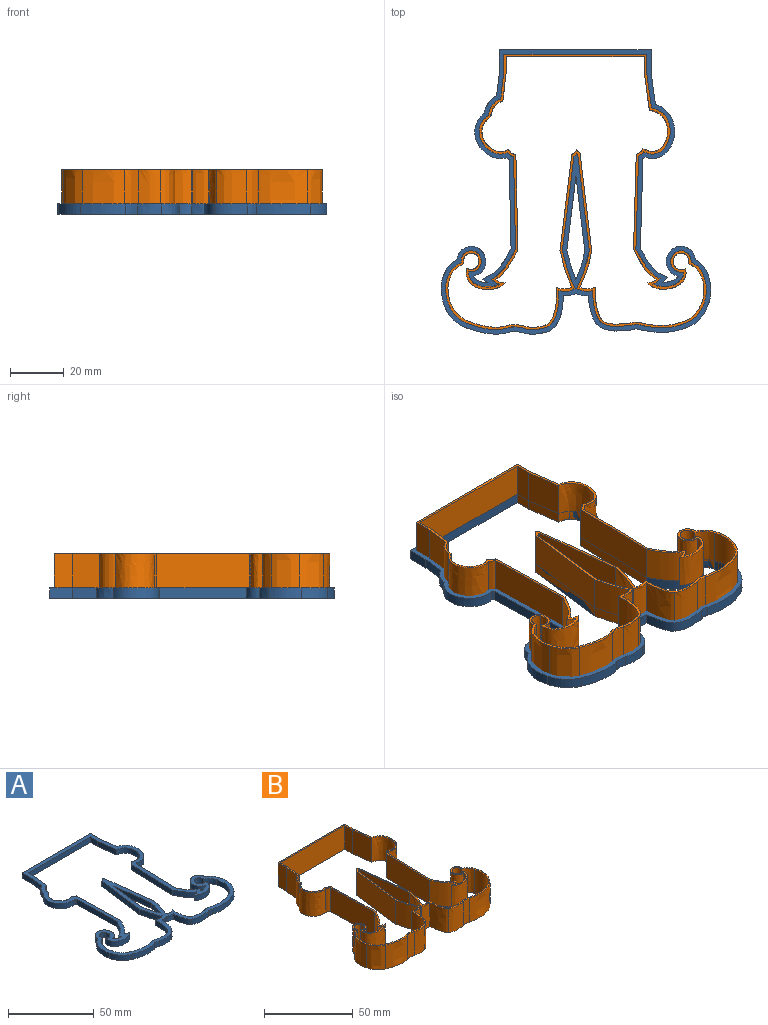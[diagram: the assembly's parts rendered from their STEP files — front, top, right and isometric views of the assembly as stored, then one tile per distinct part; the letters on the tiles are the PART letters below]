
ASSEMBLY  parts=2 mates=1
PART A: 86 faces, bbox 103.2x108.7x6.8 mm
  f0: plane 108.68x103.23mm, normal (0,0,1), area 1482.3mm2, adj f2,f3,f4,f5,f6,f7,f8,f9
  f1: plane 108.68x103.23mm, normal (0,0,-1), area 1482.3mm2, adj f2,f3,f4,f5,f6,f7,f8,f9
  f2: plane 56.38x3.81mm, normal (0,1,0), area 214.8mm2, adj f0,f1,f3,f42
  f3: extruded ~8.41x3.81mm, area 32mm2, adj f0,f1,f2,f4
  f4: plane 8.77x3.81mm, normal (-0.99,0.12,0), area 33.7mm2, adj f0,f1,f3,f5
  f5: extruded ~6.35x4.56mm, area 30.9mm2, adj f0,f1,f4,f6
  f6: extruded ~16.93x11.8mm, area 97.3mm2, adj f0,f1,f5,f7
  f7: extruded ~3.81x0.99mm, area 4.6mm2, adj f0,f1,f6,f8
  f8: plane 33.06x3.81mm, normal (-1,-0.02,0), area 126mm2, adj f0,f1,f7,f9
  f9: extruded ~11.42x10.51mm, area 60.1mm2, adj f0,f1,f8,f10
  f10: extruded ~3.81x1.86mm, area 8.5mm2, adj f0,f1,f9,f11
  f11: extruded ~5.25x3.81mm, area 23.2mm2, adj f0,f1,f10,f12
  f12: extruded ~8.33x4.46mm, area 40.7mm2, adj f0,f1,f11,f13
  f13: extruded ~10.05x5.04mm, area 52.7mm2, adj f0,f1,f12,f14
  f14: extruded ~3.81x3.75mm, area 19.4mm2, adj f0,f1,f13,f15
  f15: extruded ~11.93x3.81mm, area 47.1mm2, adj f0,f1,f14,f16
  f16: extruded ~9.71x8.12mm, area 50.1mm2, adj f0,f1,f15,f17
  f17: extruded ~16.63x3.81mm, area 65mm2, adj f0,f1,f16,f18
  f18: extruded ~4.52x3.81mm, area 17.4mm2, adj f0,f1,f17,f19
  f19: extruded ~8.96x3.81mm, area 34.7mm2, adj f0,f1,f18,f20
  f20: extruded ~13.57x6.55mm, area 61.4mm2, adj f0,f1,f19,f21
  f21: extruded ~4.56x3.81mm, area 18mm2, adj f0,f1,f20,f26
  f22: extruded ~10.98x3.81mm, area 43.8mm2, adj f0,f1,f23,f25
  f23: extruded ~27.29x3.81mm, area 104.8mm2, adj f0,f1,f22,f24
  f24: plane 27.52x3.81mm, normal (-0.99,-0.12,0), area 105.6mm2, adj f0,f1,f23,f25
  f25: extruded ~10.76x3.81mm, area 43mm2, adj f0,f1,f22,f24
  f26: extruded ~4.69x3.81mm, area 18.5mm2, adj f0,f1,f21,f27
  f27: extruded ~11.15x3.81mm, area 45.8mm2, adj f0,f1,f26,f28
  f28: extruded ~12.33x3.81mm, area 48.6mm2, adj f0,f1,f27,f29
  f29: extruded ~3.81x3.5mm, area 13.6mm2, adj f0,f1,f28,f30
  f30: extruded ~19.78x3.81mm, area 77.6mm2, adj f0,f1,f29,f31
  f31: extruded ~17.92x6.26mm, area 76.2mm2, adj f0,f1,f30,f32
  f32: extruded ~6.17x4.86mm, area 30.7mm2, adj f0,f1,f31,f33
  f33: extruded ~8.38x4.81mm, area 42.1mm2, adj f0,f1,f32,f34
  f34: extruded ~10.27x4.45mm, area 50.1mm2, adj f0,f1,f33,f35
  f35: extruded ~5.73x3.81mm, area 24.4mm2, adj f0,f1,f34,f36
  f36: extruded ~3.81x1.89mm, area 10.2mm2, adj f0,f1,f35,f37
  f37: extruded ~10.79x10.2mm, area 58.1mm2, adj f0,f1,f36,f38
  f38: plane 33.28x3.81mm, normal (1,-0.03,0), area 126.8mm2, adj f0,f1,f37,f39
  f39: extruded ~3.81x0.75mm, area 3.6mm2, adj f0,f1,f38,f40
  f40: extruded ~20.12x11.02mm, area 116.3mm2, adj f0,f1,f39,f41
  f41: plane 11.91x3.81mm, normal (0.99,0.14,0), area 45.8mm2, adj f0,f1,f40,f42
  f42: plane 8.39x3.81mm, normal (1,0,0), area 32mm2, adj f0,f1,f2,f41
  f43: plane 51.3x3.81mm, normal (0,-1,0), area 195.5mm2, adj f0,f1,f44,f85
  f44: extruded ~6.02x3.81mm, area 22.9mm2, adj f0,f1,f43,f45
  f45: plane 10.52x3.81mm, normal (0.99,-0.12,0), area 40.4mm2, adj f0,f1,f44,f46
  f46: extruded ~5.82x4.46mm, area 30.2mm2, adj f0,f1,f45,f47
  f47: extruded ~13.01x9.97mm, area 80.5mm2, adj f0,f1,f46,f48
  f48: extruded ~3.81x2.78mm, area 13.4mm2, adj f0,f1,f47,f49
  f49: plane 35.56x3.81mm, normal (1,0.02,0), area 135.5mm2, adj f0,f1,f48,f50
  f50: extruded ~10.86x8.36mm, area 52.9mm2, adj f0,f1,f49,f51
  f51: extruded ~3.81x3.57mm, area 14.5mm2, adj f0,f1,f50,f52
  f52: extruded ~14.41x7.97mm, area 77mm2, adj f0,f1,f51,f53
  f53: extruded ~4.76x4.43mm, area 31.1mm2, adj f0,f1,f52,f54
  f54: extruded ~5.25x3.97mm, area 32.2mm2, adj f0,f1,f53,f55
  f55: extruded ~4.17x3.81mm, area 20.2mm2, adj f0,f1,f54,f56
  f56: extruded ~9.97x3.81mm, area 39.4mm2, adj f0,f1,f55,f57
  f57: extruded ~8.02x6.62mm, area 41.2mm2, adj f0,f1,f56,f58
  f58: extruded ~14.83x3.81mm, area 57.9mm2, adj f0,f1,f57,f59
  f59: extruded ~5.97x3.81mm, area 23.1mm2, adj f0,f1,f58,f60
  f60: extruded ~7.76x3.81mm, area 30mm2, adj f0,f1,f59,f61
  f61: extruded ~14.21x4.62mm, area 60.5mm2, adj f0,f1,f60,f62
  f62: extruded ~5.76x3.81mm, area 22.6mm2, adj f0,f1,f61,f63
  f63: extruded ~13.75x4.44mm, area 55.2mm2, adj f0,f1,f62,f64
  f64: extruded ~35.66x4.39mm, area 136.9mm2, adj f0,f1,f63,f65
  f65: extruded ~3.81x1.89mm, area 10.3mm2, adj f0,f1,f64,f66
  f66: extruded ~3.81x1.21mm, area 6.5mm2, adj f0,f1,f65,f67
  f67: plane 36.44x4.36mm, normal (0.99,0.12,0), area 139.8mm2, adj f0,f1,f66,f68
  f68: extruded ~13.61x4.4mm, area 54.7mm2, adj f0,f1,f67,f69
  f69: extruded ~5.8x3.81mm, area 22.6mm2, adj f0,f1,f68,f70
  f70: extruded ~12.2x3.81mm, area 48.6mm2, adj f0,f1,f69,f71
  f71: extruded ~10.18x3.81mm, area 40mm2, adj f0,f1,f70,f72
  f72: extruded ~4.84x3.81mm, area 18.8mm2, adj f0,f1,f71,f73
  f73: extruded ~17.7x3.81mm, area 69.4mm2, adj f0,f1,f72,f74
  f74: extruded ~14.97x5.1mm, area 63.4mm2, adj f0,f1,f73,f75
  f75: extruded ~5.37x5.08mm, area 29.3mm2, adj f0,f1,f74,f76
  f76: extruded ~4.44x3.87mm, area 27.1mm2, adj f0,f1,f75,f77
  f77: extruded ~5.78x4.66mm, area 36.4mm2, adj f0,f1,f76,f78
  f78: extruded ~14.27x7.55mm, area 74.3mm2, adj f0,f1,f77,f79
  f79: extruded ~3.81x3.13mm, area 13.1mm2, adj f0,f1,f78,f80
  f80: extruded ~10.98x8.38mm, area 53.4mm2, adj f0,f1,f79,f81
  f81: plane 35.45x3.81mm, normal (-1,0.03,0), area 135.1mm2, adj f0,f1,f80,f82
  f82: extruded ~3.81x2.47mm, area 12.9mm2, adj f0,f1,f81,f83
  f83: extruded ~15.48x9.26mm, area 98.4mm2, adj f0,f1,f82,f84
  f84: plane 13.84x3.81mm, normal (-0.99,-0.14,0), area 53.2mm2, adj f0,f1,f83,f85
  f85: plane 6.02x3.81mm, normal (-1,0,0), area 22.9mm2, adj f0,f1,f43,f84
PART B: 88 faces, bbox 99.2x104.6x18.7 mm
  f0: plane 104.63x99.18mm, normal (0,0,1), area 523.1mm2, adj f2,f3,f4,f5,f6,f7,f8,f9
  f1: plane 104.63x99.18mm, normal (0,0,-1), area 523.1mm2, adj f2,f3,f4,f5,f6,f7,f8,f9
  f2: plane 53.08x16.51mm, normal (0,1,0), area 876.3mm2, adj f0,f1,f3,f44
  f3: extruded ~16.51x6.86mm, area 113.2mm2, adj f0,f1,f2,f4
  f4: plane 16.51x9.84mm, normal (-0.99,0.12,0), area 163.6mm2, adj f0,f1,f3,f5
  f5: extruded ~16.51x6.07mm, area 132.5mm2, adj f0,f1,f4,f6
  f6: extruded ~16.51x14.39mm, area 373.1mm2, adj f0,f1,f5,f7
  f7: extruded ~16.51x2.18mm, area 44.5mm2, adj f0,f1,f6,f8
  f8: plane 34.58x16.51mm, normal (-1,-0.02,0), area 571mm2, adj f0,f1,f7,f9
  f9: extruded ~16.51x11.06mm, area 240.5mm2, adj f0,f1,f8,f10
  f10: extruded ~16.51x3.19mm, area 60.3mm2, adj f0,f1,f9,f11
  f11: extruded ~16.51x11.51mm, area 247.1mm2, adj f0,f1,f10,f12
  f12: extruded ~16.51x6.04mm, area 151.8mm2, adj f0,f1,f11,f13
  f13: extruded ~16.51x6.94mm, area 170.5mm2, adj f0,f1,f12,f14
  f14: extruded ~16.51x3.97mm, area 85.5mm2, adj f0,f1,f13,f15
  f15: extruded ~16.51x10.66mm, area 182.4mm2, adj f0,f1,f14,f16
  f16: extruded ~16.51x8.61mm, area 192mm2, adj f0,f1,f15,f17
  f17: extruded ~16.51x15.46mm, area 261.8mm2, adj f0,f1,f16,f18
  f18: extruded ~16.51x5.46mm, area 91.6mm2, adj f0,f1,f17,f19
  f19: extruded ~16.51x8.18mm, area 137.2mm2, adj f0,f1,f18,f20
  f20: extruded ~16.51x13.87mm, area 262mm2, adj f0,f1,f19,f21
  f21: extruded ~16.51x5.98mm, area 102.7mm2, adj f0,f1,f20,f22
  f22: extruded ~16.51x14.15mm, area 246.9mm2, adj f0,f1,f21,f23
  f23: extruded ~35.03x16.51mm, area 582.7mm2, adj f0,f1,f22,f24
  f24: extruded ~16.51x1.12mm, area 24mm2, adj f0,f1,f23,f25
  f25: extruded ~16.51x0.26mm, area 5.5mm2, adj f0,f1,f24,f26
  f26: plane 35.91x16.51mm, normal (-0.99,-0.12,0), area 597.2mm2, adj f0,f1,f25,f27
  f27: extruded ~16.51x14.09mm, area 246.2mm2, adj f0,f1,f26,f28
  f28: extruded ~16.51x5.99mm, area 101.8mm2, adj f0,f1,f27,f29
  f29: extruded ~16.51x11.73mm, area 204.5mm2, adj f0,f1,f28,f30
  f30: extruded ~16.51x10.93mm, area 186.3mm2, adj f0,f1,f29,f31
  f31: extruded ~16.51x4.37mm, area 74mm2, adj f0,f1,f30,f32
  f32: extruded ~18.43x16.51mm, area 313.3mm2, adj f0,f1,f31,f33
  f33: extruded ~16.51x16mm, area 294.1mm2, adj f0,f1,f32,f34
  f34: extruded ~16.51x5.64mm, area 127.5mm2, adj f0,f1,f33,f35
  f35: extruded ~16.51x5.84mm, area 140.3mm2, adj f0,f1,f34,f36
  f36: extruded ~16.51x7.41mm, area 182.3mm2, adj f0,f1,f35,f37
  f37: extruded ~16.51x11.51mm, area 240.2mm2, adj f0,f1,f36,f38
  f38: extruded ~16.51x2.79mm, area 57.7mm2, adj f0,f1,f37,f39
  f39: extruded ~16.51x10.91mm, area 239.4mm2, adj f0,f1,f38,f40
  f40: plane 34.63x16.51mm, normal (1,-0.03,0), area 571.9mm2, adj f0,f1,f39,f41
  f41: extruded ~16.51x1.92mm, area 41.7mm2, adj f0,f1,f40,f42
  f42: extruded ~17.14x16.51mm, area 452.2mm2, adj f0,f1,f41,f43
  f43: plane 16.51x13.13mm, normal (0.99,0.14,0), area 218.8mm2, adj f0,f1,f42,f44
  f44: plane 16.51x6.85mm, normal (1,0,0), area 113.1mm2, adj f0,f1,f2,f43
  f45: plane 51.3x16.51mm, normal (0,-1,0), area 847mm2, adj f0,f1,f46,f87
  f46: extruded ~16.51x6.02mm, area 99.4mm2, adj f0,f1,f45,f47
  f47: plane 16.51x10.52mm, normal (0.99,-0.12,0), area 175mm2, adj f0,f1,f46,f48
  f48: extruded ~16.51x5.82mm, area 131mm2, adj f0,f1,f47,f49
  f49: extruded ~16.51x13.01mm, area 349mm2, adj f0,f1,f48,f50
  f50: extruded ~16.51x2.78mm, area 58.1mm2, adj f0,f1,f49,f51
  f51: plane 35.56x16.51mm, normal (1,0.02,0), area 587.3mm2, adj f0,f1,f50,f52
  f52: extruded ~16.51x10.86mm, area 229.1mm2, adj f0,f1,f51,f53
  f53: extruded ~16.51x3.57mm, area 62.8mm2, adj f0,f1,f52,f54
  f54: extruded ~16.51x14.41mm, area 333.8mm2, adj f0,f1,f53,f55
  f55: extruded ~16.51x4.76mm, area 134.8mm2, adj f0,f1,f54,f56
  f56: extruded ~16.51x5.25mm, area 139.7mm2, adj f0,f1,f55,f57
  f57: extruded ~16.51x4.17mm, area 87.7mm2, adj f0,f1,f56,f58
  f58: extruded ~16.51x9.97mm, area 170.7mm2, adj f0,f1,f57,f59
  f59: extruded ~16.51x8.02mm, area 178.4mm2, adj f0,f1,f58,f60
  f60: extruded ~16.51x14.83mm, area 251.1mm2, adj f0,f1,f59,f61
  f61: extruded ~16.51x5.97mm, area 100mm2, adj f0,f1,f60,f62
  f62: extruded ~16.51x7.76mm, area 130.1mm2, adj f0,f1,f61,f63
  f63: extruded ~16.51x14.21mm, area 262.2mm2, adj f0,f1,f62,f64
  f64: extruded ~16.51x5.76mm, area 97.8mm2, adj f0,f1,f63,f65
  f65: extruded ~16.51x13.75mm, area 239.1mm2, adj f0,f1,f64,f66
  f66: extruded ~35.66x16.51mm, area 593.2mm2, adj f0,f1,f65,f67
  f67: extruded ~16.51x1.89mm, area 44.6mm2, adj f0,f1,f66,f68
  f68: extruded ~16.51x1.21mm, area 28.1mm2, adj f0,f1,f67,f69
  f69: plane 36.44x16.51mm, normal (0.99,0.12,0), area 605.8mm2, adj f0,f1,f68,f70
  f70: extruded ~16.51x13.61mm, area 237mm2, adj f0,f1,f69,f71
  f71: extruded ~16.51x5.8mm, area 98.1mm2, adj f0,f1,f70,f72
  f72: extruded ~16.51x12.2mm, area 210.5mm2, adj f0,f1,f71,f73
  f73: extruded ~16.51x10.18mm, area 173.3mm2, adj f0,f1,f72,f74
  f74: extruded ~16.51x4.84mm, area 81.7mm2, adj f0,f1,f73,f75
  f75: extruded ~17.7x16.51mm, area 300.8mm2, adj f0,f1,f74,f76
  f76: extruded ~16.51x14.97mm, area 274.8mm2, adj f0,f1,f75,f77
  f77: extruded ~16.51x5.37mm, area 127mm2, adj f0,f1,f76,f78
  f78: extruded ~16.51x4.44mm, area 117.6mm2, adj f0,f1,f77,f79
  f79: extruded ~16.51x5.78mm, area 157.9mm2, adj f0,f1,f78,f80
  f80: extruded ~16.51x14.27mm, area 321.8mm2, adj f0,f1,f79,f81
  f81: extruded ~16.51x3.13mm, area 56.9mm2, adj f0,f1,f80,f82
  f82: extruded ~16.51x10.98mm, area 231.4mm2, adj f0,f1,f81,f83
  f83: plane 35.45x16.51mm, normal (-1,0.03,0), area 585.5mm2, adj f0,f1,f82,f84
  f84: extruded ~16.51x2.47mm, area 56.1mm2, adj f0,f1,f83,f85
  f85: extruded ~16.51x15.48mm, area 426.3mm2, adj f0,f1,f84,f86
  f86: plane 16.51x13.84mm, normal (-0.99,-0.14,0), area 230.6mm2, adj f0,f1,f85,f87
  f87: plane 16.51x6.02mm, normal (-1,0,0), area 99.4mm2, adj f0,f1,f45,f86
PLACE A at identity
PLACE B t=(110.09,2.15,0)mm
MATE fastened B.f1 <-> A.f1  axis (0,0,-1) through (75.09,16.02,0)mm
